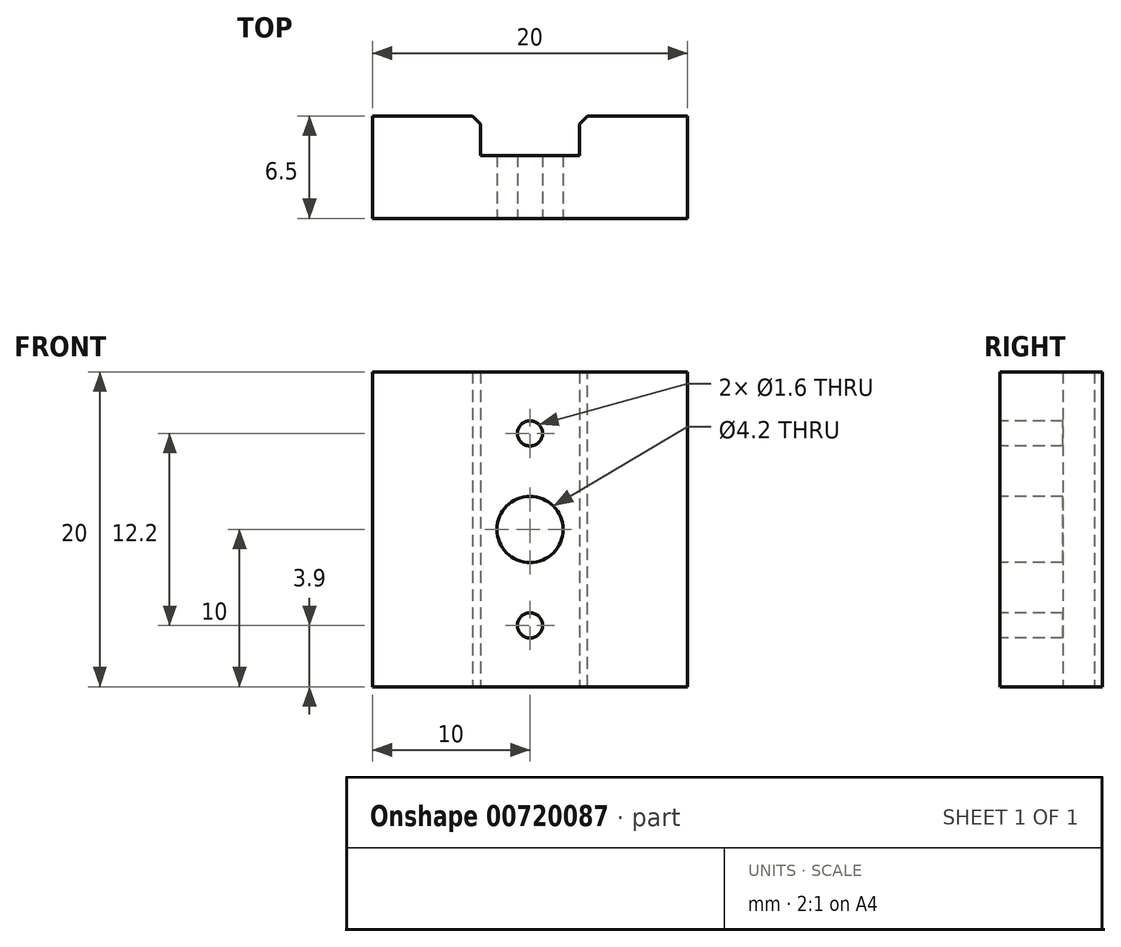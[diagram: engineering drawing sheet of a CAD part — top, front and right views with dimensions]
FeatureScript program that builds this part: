
annotation { "Feature Type Name" : "Feature", "Feature Type Description" : "" }
export const myFeature = defineFeature(function(context is Context, id is Id, definition is map)
    precondition{}
    {
        {
            var Q0;
            Q0=qCreatedBy(makeId("Top.planeOp"),FACE);
            var sketch = newSketch(context, id + "F0", { "sketchPlane" : qUnion([Q0])});
            skLineSegment(sketch, "E0.bottom", {"start": v(10, -3.25) * mm, "end": v(-10, -3.25) * mm});
            skLineSegment(sketch, "E0.top", {"start": v(10, 3.25) * mm, "end": v(3.15, 3.25) * mm});
            skLineSegment(sketch, "E0.left", {"start": v(10, -3.25) * mm, "end": v(10, 3.25) * mm});
            skLineSegment(sketch, "E0.right", {"start": v(-10, -3.25) * mm, "end": v(-10, 3.25) * mm});
            skPoint(sketch, "E0.middle", {"position": v(0, 0) * mm});
            skLineSegment(sketch, "E1.bottom", {"start": v(3.15, 0.75) * mm, "end": v(-3.15, 0.75) * mm});
            skLineSegment(sketch, "E1.left", {"start": v(3.15, 0.75) * mm, "end": v(3.15, 3.25) * mm});
            skLineSegment(sketch, "E1.right", {"start": v(-3.15, 0.75) * mm, "end": v(-3.15, 3.25) * mm});
            skPoint(sketch, "E1.middle", {"position": v(0, 3.25) * mm});
            skLineSegment(sketch, "E2.trimOffspring", {"start": v(-3.15, 3.25) * mm, "end": v(-10, 3.25) * mm});
            skPoint(sketch, "E1.top.start.orphan", {"position": v(3.15, 5.75) * mm});
            skPoint(sketch, "E3.orphan", {"position": v(-3.15, 5.75) * mm});
            skSolve(sketch);
        }
        {
            var Q0;
            Q0=makeQuery(id+"F0.imprint","IMPRINT",FACE,{"disambiguationData":[TD([[makeQuery(id+"F0.imprint","IMPRINT",EDGE,{"derivedFrom":sQuery(id+"F0.wireOp",EDGE,"E0.bottom")}),-1.0]])]});
            extrude(context, id + "F1", {"entities" : qUnion([Q0]), "endBound" : BoundingType.SYMMETRIC, "depth" : 20 * mm, "offsetDistance" : 25 * mm});
        }
        {
            var Q0;
            Q0=makeQuery(id+"F1.opExtrude","SWEPT_FACE",FACE,{"disambiguationData":[OSD([sQuery(id+"F0.wireOp",EDGE,"E0.bottom")])]});
            var sketch = newSketch(context, id + "F2", { "sketchPlane" : qUnion([Q0])});
            skCircle(sketch, "E4", {"center": v(0, 0) * mm, "radius": 2.1 * mm});
            skCircle(sketch, "E5", {"center": v(0, 6.1) * mm, "radius": 0.8 * mm});
            skCircle(sketch, "E6", {"center": v(0, -6.1) * mm, "radius": 0.8 * mm});
            skSolve(sketch);
        }
        {
            var Q0;
            Q0=sQuery(id+"F2.wireOp",VERTEX,"E5.center");
            var Q1;
            Q1=sQuery(id+"F2.wireOp",VERTEX,"E6.center");
            var Q2;
            Q2=makeQuery(id+"F1.opExtrude","SWEPT_BODY",BODY,{"disambiguationData":[OSD([sQuery(id+"F0.wireOp",EDGE,"E0.bottom"),sQuery(id+"F0.wireOp",EDGE,"E0.top"),sQuery(id+"F0.wireOp",EDGE,"E0.left"),sQuery(id+"F0.wireOp",EDGE,"E0.right"),sQuery(id+"F0.wireOp",EDGE,"E1.bottom"),sQuery(id+"F0.wireOp",EDGE,"E1.left"),sQuery(id+"F0.wireOp",EDGE,"E1.right"),sQuery(id+"F0.wireOp",EDGE,"E2.trimOffspring")])]});
            hole(context, id + "F3", {"style" : HoleStyle.SIMPLE, "endStyle" : HoleEndStyle.BLIND, "holeDiameter" : 1.6 * mm, "majorDiameter" : 4 * mm, "holeDepth" : 6 * mm, "isTappedThrough" : true, "tappedDepth" : 3.9 * mm, "tapClearance" : 3, "locations" : qUnion([Q0, Q1]), "scope" : qUnion([Q2])});
        }
        {
            var Q0;
            Q0=makeQuery(id+"F2.imprint","IMPRINT",FACE,{"disambiguationData":[TD([[makeQuery(id+"F2.imprint","IMPRINT",EDGE,{"derivedFrom":sQuery(id+"F2.wireOp",EDGE,"E4")}),1.0]])]});
            extrude(context, id + "F4", {"entities" : qUnion([Q0]), "operationType" : NewBodyOperationType.REMOVE, "oppositeDirection" : true, "depth" : 25 * mm, "offsetDistance" : 25 * mm});
        }
        {
            var Q0;
            Q0=makeQuery(id+"F1.opExtrude","SWEPT_EDGE",EDGE,{"disambiguationData":[OSD([sQuery(id+"F0.wireOp",EDGE,"E1.right"),sQuery(id+"F0.wireOp",EDGE,"E2.trimOffspring")])]});
            var Q1;
            Q1=makeQuery(id+"F1.opExtrude","SWEPT_EDGE",EDGE,{"disambiguationData":[OSD([sQuery(id+"F0.wireOp",EDGE,"E0.top"),sQuery(id+"F0.wireOp",EDGE,"E1.left")])]});
            chamfer(context, id + "F5", {"entities" : qUnion([Q0, Q1]), "width" : .5 * mm, "tangentPropagation" : true});
        }
    });
